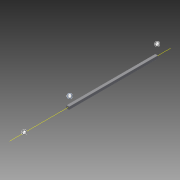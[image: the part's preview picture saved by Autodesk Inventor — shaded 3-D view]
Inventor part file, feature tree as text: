
AUTODESK INVENTOR PART (.ipt)
format: ipt  version: 2015 (Build 190159000, 159)  size: 157,696 bytes
history: native  units: in
note: dims shown in document units (in); Inventor stores cm internally (conversion verified against a paired STEP export)
features: other x6, extrude x1, imported_body x1, sketch x1
ambient origin geometry x8: Origin, YZ Plane, XZ Plane, XY Plane, X Axis, Y Axis, Z Axis, Center Point
bodies: Body1 (feature_tree)
feature tree (9):
  other  "Shaft 4.0 inch"
  parser-record x1  (decoder bookkeeping rows leaked as tree rows — omitted from the tree; the rows remain in map.json)
  other  "Shaft"
  extrude  "length cut"  Depth=4.0in
  other  "front plane"
  imported_body  "Base1"
  sketch  "Sketch1"  dims[d1=0.0in d2=4.0in d3=0.0in d4=0.0in d5=0.0in]
  other  "main axis"
  other  "back plane"
